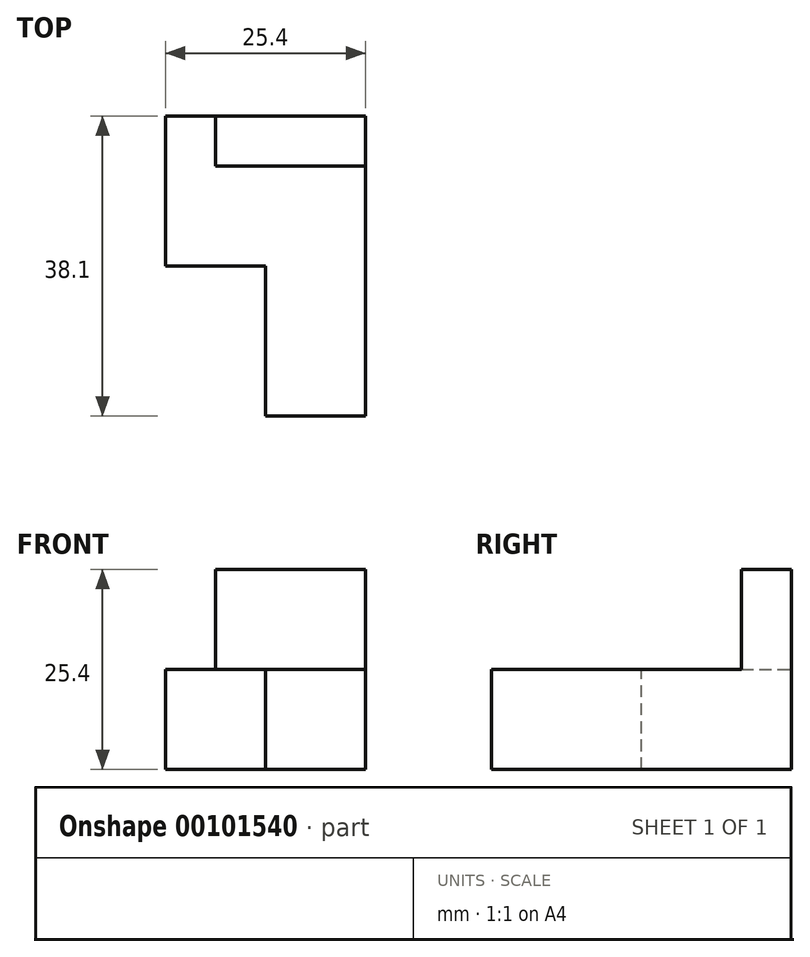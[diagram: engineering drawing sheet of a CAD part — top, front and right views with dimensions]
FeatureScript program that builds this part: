
annotation { "Feature Type Name" : "Feature", "Feature Type Description" : "" }
export const myFeature = defineFeature(function(context is Context, id is Id, definition is map)
    precondition{}
    {
        {
            var Q0;
            Q0=qCreatedBy(makeId("Top.planeOp"),FACE);
            var sketch = newSketch(context, id + "F0", { "sketchPlane" : qUnion([Q0])});
            skLineSegment(sketch, "E0", {"start": v(0, 0) * mm, "end": v(25.4, 0) * mm});
            skLineSegment(sketch, "E1", {"start": v(25.4, 0) * mm, "end": v(25.4, -38.1) * mm});
            skLineSegment(sketch, "E2", {"start": v(25.4, -38.1) * mm, "end": v(12.7, -38.1) * mm});
            skLineSegment(sketch, "E3", {"start": v(12.7, -38.1) * mm, "end": v(12.7, -19.05) * mm});
            skLineSegment(sketch, "E4", {"start": v(12.7, -19.05) * mm, "end": v(0, -19.05) * mm});
            skLineSegment(sketch, "E5", {"start": v(0, -19.05) * mm, "end": v(0, 0) * mm});
            skSolve(sketch);
        }
        {
            var Q0;
            Q0=makeQuery(id+"F0.imprint","IMPRINT",FACE,{"disambiguationData":[TD([[makeQuery(id+"F0.imprint","IMPRINT",EDGE,{"derivedFrom":sQuery(id+"F0.wireOp",EDGE,"E0")}),-1.0]])]});
            extrude(context, id + "F1", {"entities" : qUnion([Q0]), "oppositeDirection" : true, "depth" : 12.7 * mm});
        }
        {
            var Q0;
            Q0=qCreatedBy(makeId("Right.planeOp"),FACE);
            var sketch = newSketch(context, id + "F2", { "sketchPlane" : qUnion([Q0])});
            skLineSegment(sketch, "E6.bottom", {"start": v(-6.35, 0) * mm, "end": v(0, 0) * mm});
            skLineSegment(sketch, "E6.top", {"start": v(-6.35, 12.7) * mm, "end": v(0, 12.7) * mm});
            skLineSegment(sketch, "E6.left", {"start": v(-6.35, 0) * mm, "end": v(-6.35, 12.7) * mm});
            skLineSegment(sketch, "E6.right", {"start": v(0, 0) * mm, "end": v(0, 12.7) * mm});
            skSolve(sketch);
        }
        {
            var Q0;
            Q0=makeQuery(id+"F2.imprint","IMPRINT",FACE,{"disambiguationData":[TD([[makeQuery(id+"F2.imprint","IMPRINT",EDGE,{"derivedFrom":sQuery(id+"F2.wireOp",EDGE,"E6.bottom")}),1.0]])]});
            extrude(context, id + "F3", {"entities" : qUnion([Q0]), "operationType" : NewBodyOperationType.ADD, "depth" : 25.4 * mm, "hasSecondDirection" : true, "secondDirectionOppositeDirection" : false, "secondDirectionDepth" : 6.35 * mm});
        }
    });
